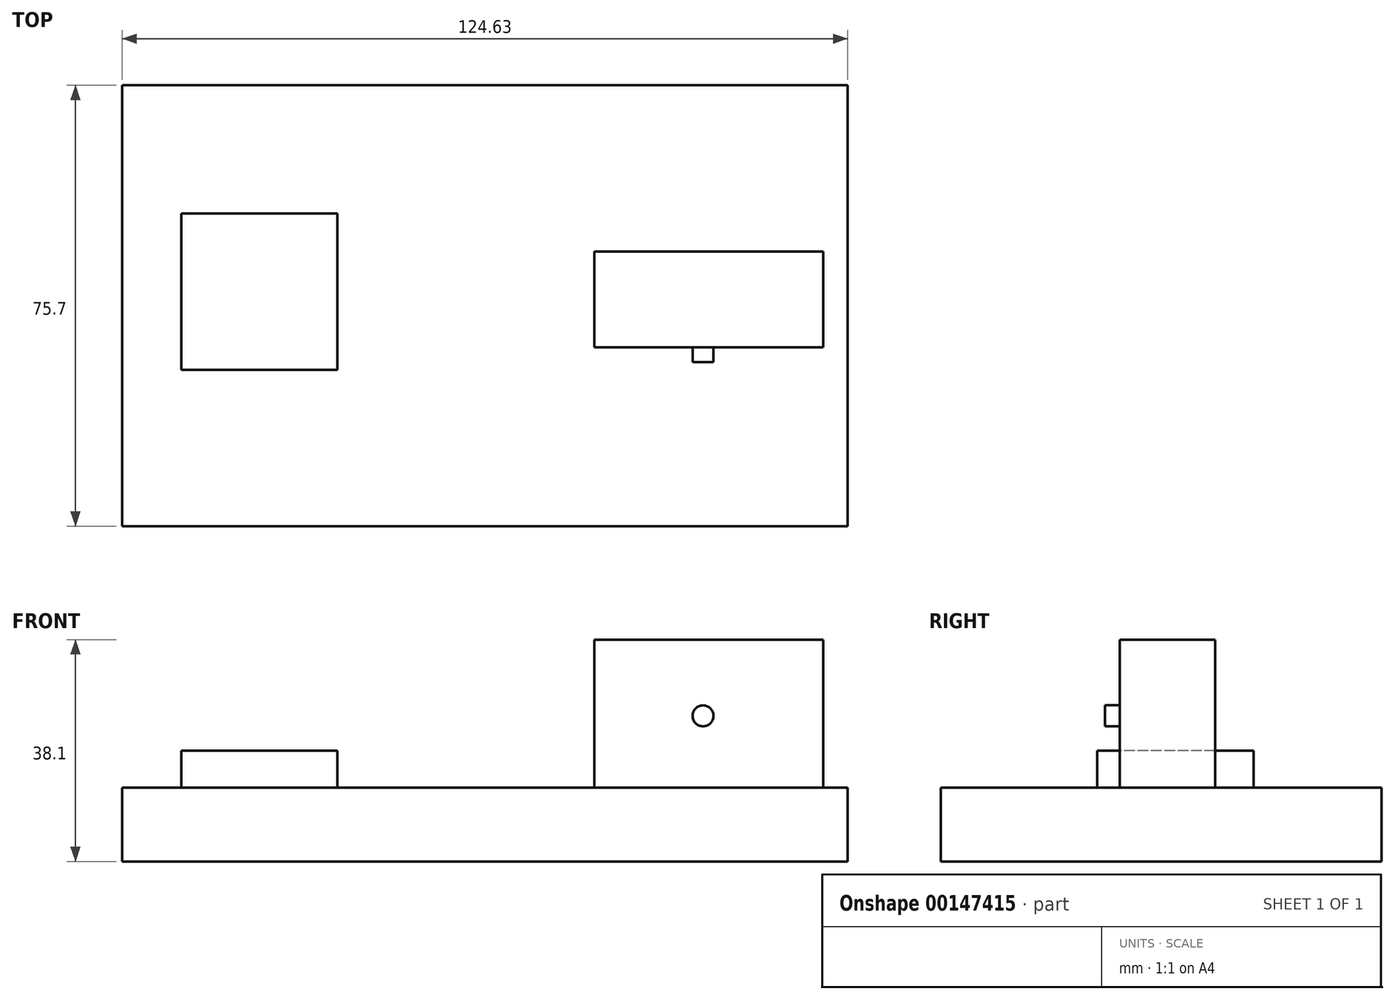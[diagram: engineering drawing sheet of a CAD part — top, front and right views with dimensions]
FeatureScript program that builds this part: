
annotation { "Feature Type Name" : "Feature", "Feature Type Description" : "" }
export const myFeature = defineFeature(function(context is Context, id is Id, definition is map)
    precondition{}
    {
        {
            var Q0;
            Q0=qCreatedBy(makeId("Top.planeOp"),FACE);
            var sketch = newSketch(context, id + "F0", { "sketchPlane" : qUnion([Q0])});
            skLineSegment(sketch, "E0.bottom", {"start": v(-58.16, 34.39) * mm, "end": v(66.47, 34.39) * mm});
            skLineSegment(sketch, "E0.top", {"start": v(-58.16, -41.31) * mm, "end": v(66.47, -41.31) * mm});
            skLineSegment(sketch, "E0.left", {"start": v(-58.16, 34.39) * mm, "end": v(-58.16, -41.31) * mm});
            skLineSegment(sketch, "E0.right", {"start": v(66.47, 34.39) * mm, "end": v(66.47, -41.31) * mm});
            skSolve(sketch);
        }
        {
            var Q0;
            Q0 = qSketchRegion(id + "F0", true);
            extrude(context, id + "F1", {"entities" : qUnion([Q0]), "depth" : 12.7 * mm});
        }
        {
            var Q0;
            Q0=makeQuery(id+"F1.opExtrude","CAP_FACE",FACE,{"disambiguationData":[OSD([sQuery(id+"F0.wireOp",EDGE,"E0.bottom"),sQuery(id+"F0.wireOp",EDGE,"E0.top"),sQuery(id+"F0.wireOp",EDGE,"E0.left"),sQuery(id+"F0.wireOp",EDGE,"E0.right")])],"isStart":false});
            var sketch = newSketch(context, id + "F2", { "sketchPlane" : qUnion([Q0])});
            skLineSegment(sketch, "E1.bottom", {"start": v(62.28, 5.81) * mm, "end": v(22.95, 5.81) * mm});
            skLineSegment(sketch, "E1.top", {"start": v(62.28, -10.58) * mm, "end": v(22.95, -10.58) * mm});
            skLineSegment(sketch, "E1.left", {"start": v(62.28, 5.81) * mm, "end": v(62.28, -10.58) * mm});
            skLineSegment(sketch, "E1.right", {"start": v(22.95, 5.81) * mm, "end": v(22.95, -10.58) * mm});
            skSolve(sketch);
        }
        {
            var Q0;
            Q0 = qSketchRegion(id + "F2", true);
            extrude(context, id + "F3", {"entities" : qUnion([Q0]), "operationType" : NewBodyOperationType.ADD, "depth" : 25.4 * mm});
        }
        {
            var Q0;
            Q0=makeQuery(id+"F1.opExtrude","CAP_FACE",FACE,{"disambiguationData":[OSD([sQuery(id+"F0.wireOp",EDGE,"E0.bottom"),sQuery(id+"F0.wireOp",EDGE,"E0.top"),sQuery(id+"F0.wireOp",EDGE,"E0.left"),sQuery(id+"F0.wireOp",EDGE,"E0.right")])],"isStart":false});
            var sketch = newSketch(context, id + "F4", { "sketchPlane" : qUnion([Q0])});
            skLineSegment(sketch, "E2.bottom", {"start": v(-47.98, 12.37) * mm, "end": v(-21.16, 12.37) * mm});
            skLineSegment(sketch, "E2.top", {"start": v(-47.98, -14.45) * mm, "end": v(-21.16, -14.45) * mm});
            skLineSegment(sketch, "E2.left", {"start": v(-47.98, 12.37) * mm, "end": v(-47.98, -14.45) * mm});
            skLineSegment(sketch, "E2.right", {"start": v(-21.16, 12.37) * mm, "end": v(-21.16, -14.45) * mm});
            skSolve(sketch);
        }
        {
            var Q0;
            Q0 = qSketchRegion(id + "F4", true);
            extrude(context, id + "F5", {"entities" : qUnion([Q0]), "operationType" : NewBodyOperationType.ADD, "depth" : 6.35 * mm});
        }
        {
            var Q0;
            Q0=makeQuery(id+"F3.opExtrude","SWEPT_FACE",FACE,{"disambiguationData":[OSD([sQuery(id+"F2.wireOp",EDGE,"E1.top")])]});
            var sketch = newSketch(context, id + "F6", { "sketchPlane" : qUnion([Q0])});
            skCircle(sketch, "E3", {"center": v(41.62, 25.01) * mm, "radius": 1.8 * mm});
            skSolve(sketch);
        }
        {
            var Q0;
            Q0=makeQuery(id+"F6.imprint","IMPRINT",FACE,{"disambiguationData":[TD([[makeQuery(id+"F6.imprint","IMPRINT",EDGE,{"derivedFrom":sQuery(id+"F6.wireOp",EDGE,"E3")}),1.0]])]});
            extrude(context, id + "F7", {"entities" : qUnion([Q0]), "operationType" : NewBodyOperationType.ADD, "depth" : 2.54 * mm});
        }
    });
